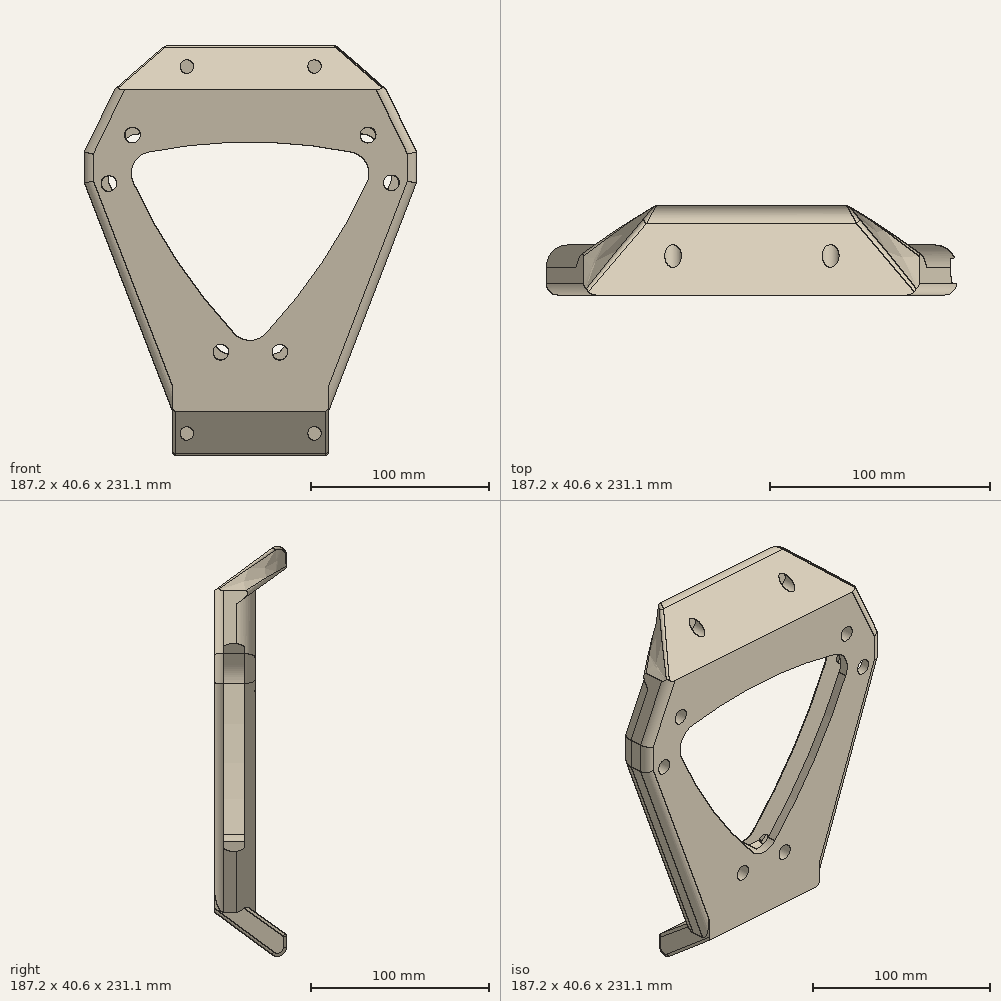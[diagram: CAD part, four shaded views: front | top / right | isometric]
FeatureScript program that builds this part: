
annotation { "Feature Type Name" : "Feature", "Feature Type Description" : "" }
export const myFeature = defineFeature(function(context is Context, id is Id, definition is map)
    precondition{}
    {
        {
            var Q0;
            Q0=qCreatedBy(makeId("Front.planeOp"),FACE);
            var sketch = newSketch(context, id + "F0", { "sketchPlane" : qUnion([Q0])});
            skArc(sketch, "E0.0", {"start": v(56.94, 46.93) * mm, "mid": v(0, 52.61) * mm, "end": v(-56.95, 46.93) * mm});
            skArc(sketch, "E1.0", {"start": v(-56.95, 46.93) * mm, "mid": v(-65.58, 40.37) * mm, "end": v(-65.8, 29.54) * mm});
            skArc(sketch, "E2.0", {"start": v(-65.8, 29.54) * mm, "mid": v(-40.83, -15.1) * mm, "end": v(-9.12, -55.22) * mm});
            skArc(sketch, "E3.0", {"start": v(-9.12, -55.22) * mm, "mid": v(0, -59.2) * mm, "end": v(9.12, -55.22) * mm});
            skArc(sketch, "E4.0", {"start": v(9.12, -55.22) * mm, "mid": v(40.83, -15.1) * mm, "end": v(65.79, 29.54) * mm});
            skArc(sketch, "E5.0", {"start": v(65.79, 29.54) * mm, "mid": v(65.57, 40.37) * mm, "end": v(56.94, 46.93) * mm});
            skPoint(sketch, "E6.startSnap0", {"position": v(-16.47, -65.9) * mm});
            skCircle(sketch, "E7", {"center": v(-16.47, -65.9) * mm, "radius": 4.45 * mm});
            skCircle(sketch, "E8", {"center": v(16.8, -65.9) * mm, "radius": 4.45 * mm});
            skPoint(sketch, "E9.startSnap0", {"position": v(-66.32, 56.49) * mm});
            skCircle(sketch, "E10", {"center": v(-66.32, 56.49) * mm, "radius": 4.45 * mm});
            skCircle(sketch, "E11", {"center": v(66.48, 56.49) * mm, "radius": 4.45 * mm});
            skCircle(sketch, "E12", {"center": v(-79.6, 29.11) * mm, "radius": 4.45 * mm});
            skPoint(sketch, "E12.centerSnap0", {"position": v(-79.6, 29.54) * mm});
            skCircle(sketch, "E13", {"center": v(79.66, 29.54) * mm, "radius": 4.45 * mm});
            skLineSegment(sketch, "E14", {"start": v(-93.4, 29.54) * mm, "end": v(-43.75, -99.08) * mm});
            skLineSegment(sketch, "E15", {"start": v(93.75, 29.54) * mm, "end": v(44.32, -99.08) * mm});
            skLineSegment(sketch, "E16", {"start": v(-43.75, -99.08) * mm, "end": v(44.32, -99.08) * mm});
            skLineSegment(sketch, "E17", {"start": v(-93.4, 29.54) * mm, "end": v(-93.4, 46.93) * mm});
            skLineSegment(sketch, "E18", {"start": v(93.75, 29.54) * mm, "end": v(93.75, 46.93) * mm});
            skLineSegment(sketch, "E19", {"start": v(-93.4, 46.93) * mm, "end": v(-76.4, 81.96) * mm});
            skLineSegment(sketch, "E20", {"start": v(-76.4, 81.96) * mm, "end": v(76.74, 81.96) * mm});
            skLineSegment(sketch, "E21", {"start": v(76.74, 81.96) * mm, "end": v(93.75, 46.93) * mm});
            skSolve(sketch);
        }
        {
            var Q0;
            Q0=qSketchRegion(id+"F0",true);
            extrude(context, id + "F1", {"entities" : qUnion([Q0]), "depth" : 22.86 * mm, "offsetDistance" : 25.4 * mm});
        }
        {
            var Q0;
            Q0=makeQuery(id+"F0.imprint","IMPRINT",FACE,{"disambiguationData":[TD([[makeQuery(id+"F0.imprint","IMPRINT",EDGE,{"derivedFrom":sQuery(id+"F0.wireOp",EDGE,"E0.0")}),1.0]])]});
            var sketch = newSketch(context, id + "F2", { "sketchPlane" : qUnion([Q0])});
            skCircle(sketch, "E22", {"center": v(-66.12, 56.3) * mm, "radius": 4.45 * mm});
            skCircle(sketch, "E23", {"center": v(-79.37, 29.04) * mm, "radius": 4.45 * mm});
            skCircle(sketch, "E24", {"center": v(-16.42, -65.73) * mm, "radius": 4.44 * mm});
            skCircle(sketch, "E25", {"center": v(16.75, -65.72) * mm, "radius": 4.45 * mm});
            skCircle(sketch, "E26", {"center": v(79.44, 29.44) * mm, "radius": 4.45 * mm});
            skCircle(sketch, "E27", {"center": v(66.3, 56.32) * mm, "radius": 4.45 * mm});
            skSolve(sketch);
        }
        {
            var Q0;
            Q0=qSketchRegion(id+"F2",true);
            extrude(context, id + "F3", {"entities" : qUnion([Q0]), "operationType" : NewBodyOperationType.ADD, "depth" : 5.08 * mm, "offsetDistance" : 25.4 * mm});
        }
        {
            var Q0;
            Q0=qCreatedBy(makeId("Front.planeOp"),FACE);
            var sketch = newSketch(context, id + "F4", { "sketchPlane" : qUnion([Q0])});
            skArc(sketch, "E28", {"start": v(66.33, 56.57) * mm, "mid": v(0, 62.5) * mm, "end": v(-66.32, 56.57) * mm});
            skArc(sketch, "E29", {"start": v(16.75, -65.82) * mm, "mid": v(52.58, -20.93) * mm, "end": v(79.32, 29.9) * mm});
            skArc(sketch, "E30", {"start": v(-79.66, 29.56) * mm, "mid": v(-52.6, -21) * mm, "end": v(-16.4, -65.48) * mm});
            skArc(sketch, "E31", {"start": v(79.32, 29.9) * mm, "mid": v(77.03, 45.29) * mm, "end": v(66.33, 56.57) * mm});
            skArc(sketch, "E32", {"start": v(-66.32, 56.57) * mm, "mid": v(-77.39, 45.23) * mm, "end": v(-79.66, 29.56) * mm});
            skArc(sketch, "E33", {"start": v(-16.4, -65.48) * mm, "mid": v(0.14, -68.94) * mm, "end": v(16.75, -65.82) * mm});
            skArc(sketch, "E34.0", {"start": v(65.56, 29.64) * mm, "mid": v(65.34, 40.26) * mm, "end": v(56.89, 46.68) * mm});
            skArc(sketch, "E34.1", {"start": v(-56.9, 46.68) * mm, "mid": v(-65.36, 40.26) * mm, "end": v(-65.57, 29.64) * mm});
            skArc(sketch, "E34.2", {"start": v(-65.57, 29.64) * mm, "mid": v(-40.62, -14.96) * mm, "end": v(-8.93, -55.05) * mm});
            skArc(sketch, "E34.3", {"start": v(56.89, 46.68) * mm, "mid": v(0, 52.36) * mm, "end": v(-56.9, 46.68) * mm});
            skArc(sketch, "E34.4", {"start": v(-8.93, -55.05) * mm, "mid": v(0, -58.94) * mm, "end": v(8.93, -55.05) * mm});
            skArc(sketch, "E34.5", {"start": v(8.93, -55.05) * mm, "mid": v(40.62, -14.96) * mm, "end": v(65.56, 29.64) * mm});
            skSolve(sketch);
        }
        {
            var Q0;
            Q0=qSketchRegion(id+"F4",true);
            extrude(context, id + "F5", {"entities" : qUnion([Q0]), "operationType" : NewBodyOperationType.REMOVE, "depth" : 5.6 * mm, "offsetDistance" : 25.4 * mm});
        }
        {
            var Q0;
            Q0=qCreatedBy(makeId("Front.planeOp"),FACE);
            cPlane(context, id + "F6", {"entities" : qUnion([Q0]), "cplaneType" : CPlaneType.OFFSET, "offset" : 17.78 * mm, "oppositeDirection" : true, "width" : 152.4 * mm, "height" : 152.4 * mm});
        }
        {
            var Q0;
            Q0=qCreatedBy(id+"F6.planeOp",FACE);
            var sketch = newSketch(context, id + "F7", { "sketchPlane" : qUnion([Q0])});
            skLineSegment(sketch, "E35.0", {"start": v(-43.75, -111.78) * mm, "end": v(44.32, -111.78) * mm});
            skLineSegment(sketch, "E36", {"start": v(44.32, -111.78) * mm, "end": v(44.32, -129.05) * mm});
            skLineSegment(sketch, "E37", {"start": v(-43.75, -111.78) * mm, "end": v(-43.75, -129.05) * mm});
            skLineSegment(sketch, "E38.0", {"start": v(-43.75, -129.05) * mm, "end": v(44.32, -129.05) * mm});
            skLineSegment(sketch, "E39.0", {"start": v(-43.75, 94.73) * mm, "end": v(44.32, 94.73) * mm});
            skLineSegment(sketch, "E40", {"start": v(44.32, 94.73) * mm, "end": v(44.32, 112) * mm});
            skLineSegment(sketch, "E41", {"start": v(-43.75, 94.73) * mm, "end": v(-43.75, 112) * mm});
            skLineSegment(sketch, "E42", {"start": v(44.32, 112) * mm, "end": v(-43.75, 112) * mm});
            skSolve(sketch);
        }
        {
            var Q1;
            Q1=makeQuery(id+"F1.opExtrude","SWEPT_FACE",FACE,{"disambiguationData":[OSD([sQuery(id+"F0.wireOp",EDGE,"E20")])]});
            var Q2;
            Q2=makeQuery(id+"F7.imprint","IMPRINT",FACE,{"disambiguationData":[TD([[makeQuery(id+"F7.imprint","IMPRINT",EDGE,{"derivedFrom":sQuery(id+"F7.wireOp",EDGE,"E39.0")}),1.0]])]});
            loft(context, id + "F8", {"operationType" : NewBodyOperationType.ADD, "sheetProfilesArray" : [{ "sheetProfileEntities" : qUnion([Q1]) }, { "sheetProfileEntities" : qUnion([Q2]) }]});
        }
        {
            var Q1;
            Q1=makeQuery(id+"F7.imprint","IMPRINT",FACE,{"disambiguationData":[TD([[makeQuery(id+"F7.imprint","IMPRINT",EDGE,{"derivedFrom":sQuery(id+"F7.wireOp",EDGE,"E35.0")}),-1.0]])]});
            var Q2;
            Q2=makeQuery(id+"F1.opExtrude","SWEPT_FACE",FACE,{"disambiguationData":[OSD([sQuery(id+"F0.wireOp",EDGE,"E16")])]});
            loft(context, id + "F9", {"operationType" : NewBodyOperationType.ADD, "sheetProfilesArray" : [{ "sheetProfileEntities" : qUnion([Q1]) }, { "sheetProfileEntities" : qUnion([Q2]) }]});
        }
        {
            var Q0;
            Q0=qCreatedBy(makeId("Front.planeOp"),FACE);
            var sketch = newSketch(context, id + "F10", { "sketchPlane" : qUnion([Q0])});
            skCircle(sketch, "E43", {"center": v(-35.62, -111.7) * mm, "radius": 3.81 * mm});
            skLineSegment(sketch, "E44", {"start": v(-43.7, -111.95) * mm, "end": v(-35.62, -111.7) * mm});
            skLineSegment(sketch, "E45", {"start": v(44.41, -111.7) * mm, "end": v(36.33, -111.7) * mm});
            skCircle(sketch, "E46", {"center": v(36.33, -111.7) * mm, "radius": 3.81 * mm});
            skCircle(sketch, "E47", {"center": v(-35.62, 95.09) * mm, "radius": 3.81 * mm});
            skCircle(sketch, "E48", {"center": v(36.33, 95.09) * mm, "radius": 3.81 * mm});
            skSolve(sketch);
        }
        {
            var Q0;
            Q0=qSketchRegion(id+"F10",true);
            extrude(context, id + "F11", {"entities" : qUnion([Q0]), "operationType" : NewBodyOperationType.REMOVE, "depth" : 12.7 * mm, "offsetDistance" : 25.4 * mm});
        }
        {
            var Q0;
            Q0=makeQuery(id+"F1.opExtrude","CAP_EDGE",EDGE,{"disambiguationData":[OSD([sQuery(id+"F0.wireOp",EDGE,"E14")])],"isStart":false});
            var Q1;
            Q1=makeQuery(id+"F1.opExtrude","CAP_EDGE",EDGE,{"disambiguationData":[OSD([sQuery(id+"F0.wireOp",EDGE,"E17")])],"isStart":false});
            var Q2;
            Q2=makeQuery(id+"F1.opExtrude","CAP_EDGE",EDGE,{"disambiguationData":[OSD([sQuery(id+"F0.wireOp",EDGE,"E19")])],"isStart":false});
            var Q3;
            Q3=makeQuery(id+"F8.opLoft","MID_CAP_EDGE",EDGE,{"disambiguationData":[OSD([sQuery(id+"F7.wireOp",EDGE,"E40"),sQuery(id+"F7.wireOp",EDGE,"E41"),sQuery(id+"F7.wireOp",EDGE,"E42")])],"capPos":1.0});
            var Q4;
            Q4=makeQuery(id+"F9.opLoft","MID_CAP_EDGE",EDGE,{"disambiguationData":[OSD([sQuery(id+"F7.wireOp",EDGE,"E36"),sQuery(id+"F7.wireOp",EDGE,"E37"),sQuery(id+"F7.wireOp",EDGE,"E38.0")])],"capPos":0.0});
            var Q5;
            Q5=makeQuery(id+"F1.opExtrude","CAP_EDGE",EDGE,{"disambiguationData":[OSD([sQuery(id+"F0.wireOp",EDGE,"E15")])],"isStart":false});
            var Q6;
            Q6=makeQuery(id+"F1.opExtrude","CAP_EDGE",EDGE,{"disambiguationData":[OSD([sQuery(id+"F0.wireOp",EDGE,"E18")])],"isStart":false});
            var Q7;
            Q7=makeQuery(id+"F1.opExtrude","CAP_EDGE",EDGE,{"disambiguationData":[OSD([sQuery(id+"F0.wireOp",EDGE,"E21")])],"isStart":false});
            fillet(context, id + "F12", {"entities" : qUnion([Q0, Q1, Q2, Q3, Q4, Q5, Q6, Q7]), "radius" : 5.08 * mm, "tangentPropagation" : true, "allowEdgeOverflow" : false});
        }
        {
            var Q0;
            Q0=makeQuery(id+"F8.opLoft","SWEPT_EDGE",EDGE,{"disambiguationData":[OSD([sQuery(id+"F0.wireOp",EDGE,"E19"),sQuery(id+"F0.wireOp",EDGE,"E20"),sQuery(id+"F7.wireOp",EDGE,"E41"),sQuery(id+"F7.wireOp",EDGE,"E42")])]});
            var Q1;
            Q1=makeQuery(id+"F9.opLoft","SWEPT_EDGE",EDGE,{"disambiguationData":[OSD([sQuery(id+"F0.wireOp",EDGE,"E14"),sQuery(id+"F0.wireOp",EDGE,"E16"),sQuery(id+"F7.wireOp",EDGE,"E37"),sQuery(id+"F7.wireOp",EDGE,"E38.0")])]});
            var Q2;
            Q2=makeQuery(id+"F8.opLoft","SWEPT_EDGE",EDGE,{"disambiguationData":[OSD([sQuery(id+"F0.wireOp",EDGE,"E20"),sQuery(id+"F0.wireOp",EDGE,"E21"),sQuery(id+"F7.wireOp",EDGE,"E40"),sQuery(id+"F7.wireOp",EDGE,"E42")])]});
            var Q3;
            Q3=makeQuery(id+"F9.opLoft","SWEPT_EDGE",EDGE,{"disambiguationData":[OSD([sQuery(id+"F0.wireOp",EDGE,"E15"),sQuery(id+"F0.wireOp",EDGE,"E16"),sQuery(id+"F7.wireOp",EDGE,"E36"),sQuery(id+"F7.wireOp",EDGE,"E38.0")])]});
            fillet(context, id + "F13", {"entities" : qUnion([Q0, Q1, Q2, Q3]), "radius" : 1.78 * mm, "tangentPropagation" : true, "allowEdgeOverflow" : false});
        }
        {
            var Q0;
            Q0=makeQuery(id+"F1.opExtrude","CAP_EDGE",EDGE,{"disambiguationData":[OSD([sQuery(id+"F0.wireOp",EDGE,"E15")])],"isStart":true});
            var Q1;
            Q1=makeQuery(id+"F1.opExtrude","CAP_EDGE",EDGE,{"disambiguationData":[OSD([sQuery(id+"F0.wireOp",EDGE,"E18")])],"isStart":true});
            var Q2;
            Q2=makeQuery(id+"F1.opExtrude","CAP_EDGE",EDGE,{"disambiguationData":[OSD([sQuery(id+"F0.wireOp",EDGE,"E21")])],"isStart":true});
            var Q3;
            Q3=makeQuery(id+"F1.opExtrude","CAP_EDGE",EDGE,{"disambiguationData":[OSD([sQuery(id+"F0.wireOp",EDGE,"E19")])],"isStart":true});
            var Q4;
            Q4=makeQuery(id+"F1.opExtrude","CAP_EDGE",EDGE,{"disambiguationData":[OSD([sQuery(id+"F0.wireOp",EDGE,"E17")])],"isStart":true});
            var Q5;
            Q5=makeQuery(id+"F1.opExtrude","CAP_EDGE",EDGE,{"disambiguationData":[OSD([sQuery(id+"F0.wireOp",EDGE,"E14")])],"isStart":true});
            fillet(context, id + "F14", {"entities" : qUnion([Q0, Q1, Q2, Q3, Q4, Q5]), "radius" : 10.16 * mm, "tangentPropagation" : true, "allowEdgeOverflow" : false});
        }
        {
            var Q0;
            Q0=makeQuery(id+"F8.opLoft","SWEPT_EDGE",EDGE,{"disambiguationData":[OSD([sQuery(id+"F0.wireOp",EDGE,"E20"),sQuery(id+"F0.wireOp",EDGE,"E21"),sQuery(id+"F7.wireOp",EDGE,"E39.0"),sQuery(id+"F7.wireOp",EDGE,"E40")])]});
            var Q1;
            Q1=makeQuery(id+"F9.opLoft","SWEPT_EDGE",EDGE,{"disambiguationData":[OSD([sQuery(id+"F0.wireOp",EDGE,"E14"),sQuery(id+"F0.wireOp",EDGE,"E16"),sQuery(id+"F7.wireOp",EDGE,"E35.0"),sQuery(id+"F7.wireOp",EDGE,"E37")])]});
            fillet(context, id + "F15", {"entities" : qUnion([Q0, Q1]), "radius" : 1.78 * mm, "tangentPropagation" : true, "allowEdgeOverflow" : false});
        }
        {
            var Q0;
            Q0=qCreatedBy(makeId("Right.planeOp"),FACE);
            var sketch = newSketch(context, id + "F16", { "sketchPlane" : qUnion([Q0])});
            skLineSegment(sketch, "E49", {"start": v(-17.53, 50.88) * mm, "end": v(-17.53, -63.38) * mm});
            skLineSegment(sketch, "E50", {"start": v(-6.15, 50.88) * mm, "end": v(-6.15, -63.38) * mm});
            skArc(sketch, "E51", {"start": v(-6.15, 50.88) * mm, "mid": v(-11.84, 52.35) * mm, "end": v(-17.53, 50.88) * mm});
            skArc(sketch, "E52", {"start": v(-17.53, -63.38) * mm, "mid": v(-11.84, -64.85) * mm, "end": v(-6.15, -63.38) * mm});
            skSolve(sketch);
        }
        {
            var Q0;
            Q0 = qSketchRegion(id + "F16", true);
            extrude(context, id + "F17", {"entities" : qUnion([Q0]), "operationType" : NewBodyOperationType.REMOVE, "depth" : 102.62 * mm, "offsetDistance" : 25.4 * mm});
        }
    });
